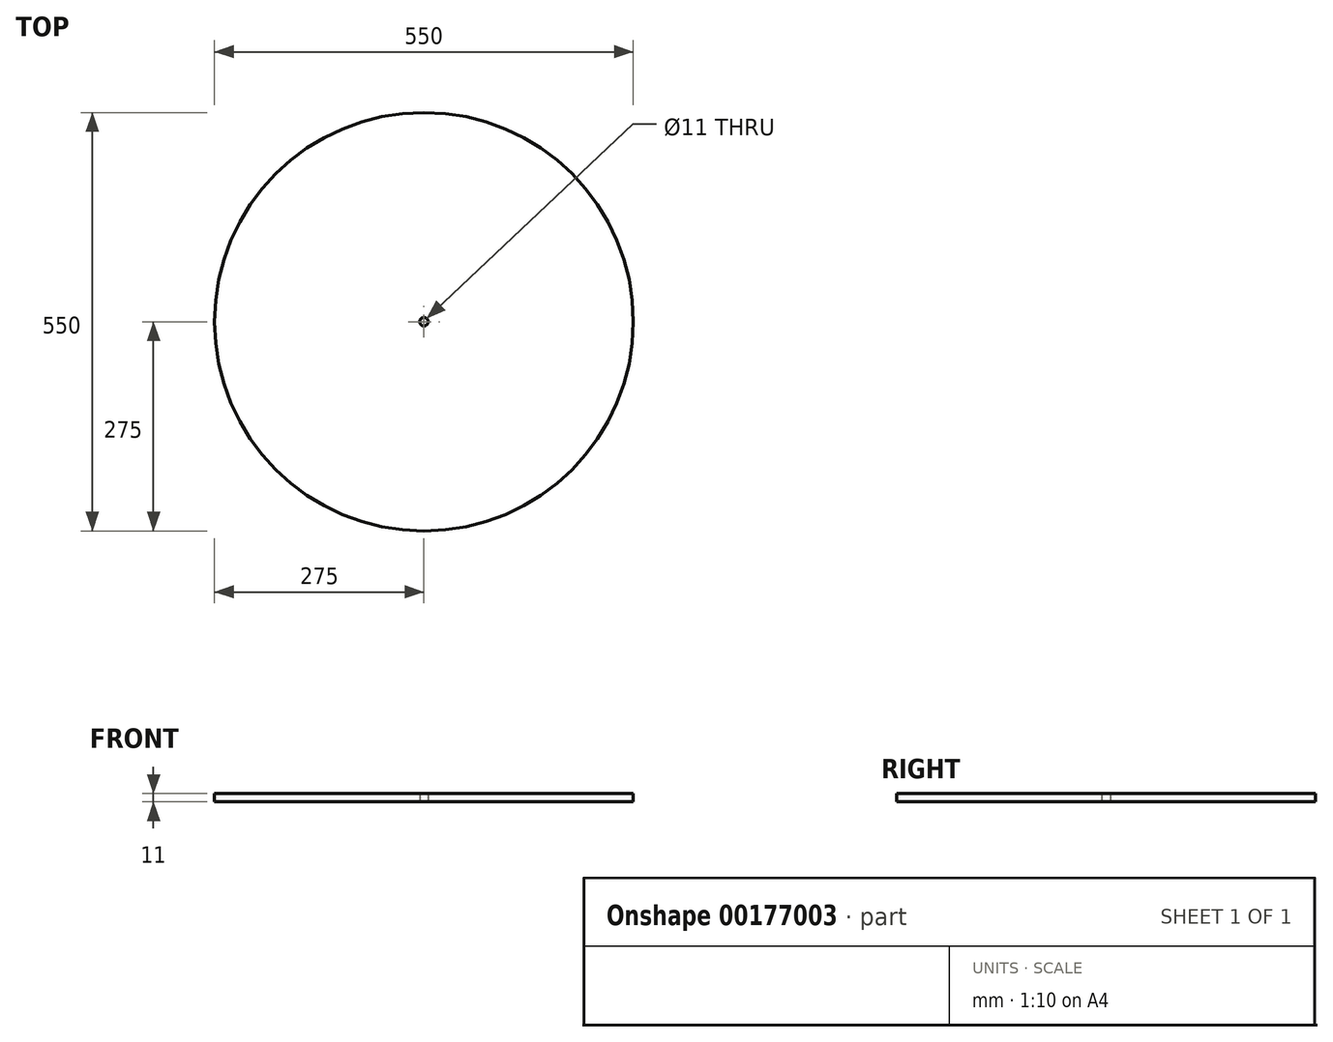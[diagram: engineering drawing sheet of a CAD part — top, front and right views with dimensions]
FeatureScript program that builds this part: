
annotation { "Feature Type Name" : "Feature", "Feature Type Description" : "" }
export const myFeature = defineFeature(function(context is Context, id is Id, definition is map)
    precondition{}
    {
        {
            var Q0;
            Q0=qCreatedBy(makeId("Top.planeOp"),FACE);
            var sketch = newSketch(context, id + "F0", { "sketchPlane" : qUnion([Q0])});
            skCircle(sketch, "E0", {"center": v(0, 0) * mm, "radius": 275 * mm});
            skCircle(sketch, "E1", {"center": v(0, 0) * mm, "radius": 5.5 * mm});
            skSolve(sketch);
        }
        {
            var Q0;
            Q0=makeQuery(id+"F0.imprint","IMPRINT",FACE,{"disambiguationData":[TD([[makeQuery(id+"F0.imprint","IMPRINT",EDGE,{"derivedFrom":sQuery(id+"F0.wireOp",EDGE,"E0")}),1.0]])]});
            extrude(context, id + "F1", {"entities" : qUnion([Q0]), "depth" : 11 * mm});
        }
    });
